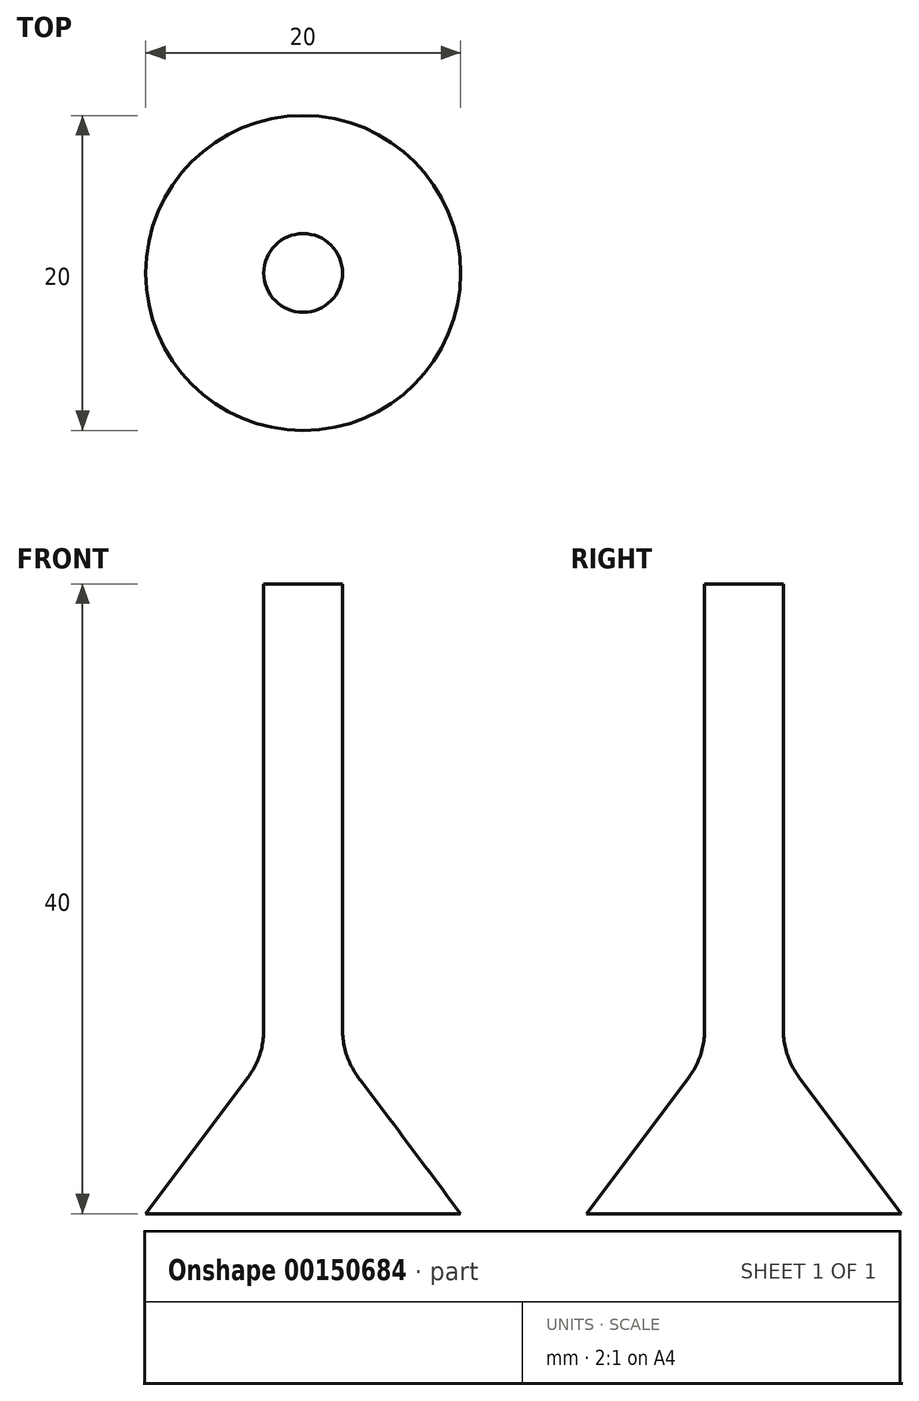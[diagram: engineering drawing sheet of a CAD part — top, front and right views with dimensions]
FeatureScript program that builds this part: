
annotation { "Feature Type Name" : "Feature", "Feature Type Description" : "" }
export const myFeature = defineFeature(function(context is Context, id is Id, definition is map)
    precondition{}
    {
        {
            var Q0;
            Q0=qCreatedBy(makeId("Front.planeOp"),FACE);
            var sketch = newSketch(context, id + "F0", { "sketchPlane" : qUnion([Q0])});
            skLineSegment(sketch, "E0.bottom", {"start": v(-2.96, 40.01) * mm, "end": v(-5.46, 40.01) * mm});
            skLineSegment(sketch, "E0.top", {"start": v(-2.96, 10.01) * mm, "end": v(-5.46, 10.01) * mm});
            skLineSegment(sketch, "E0.left", {"start": v(-2.96, 40.01) * mm, "end": v(-2.96, 10.01) * mm});
            skLineSegment(sketch, "E0.right", {"start": v(-5.46, 40.01) * mm, "end": v(-5.46, 11.68) * mm});
            skLineSegment(sketch, "E1", {"start": v(-2.96, 10.01) * mm, "end": v(-2.96, 0.01) * mm});
            skLineSegment(sketch, "E2", {"start": v(-2.96, 0.01) * mm, "end": v(-12.96, 0.01) * mm});
            skLineSegment(sketch, "E3", {"start": v(-12.96, 0.01) * mm, "end": v(-6.46, 8.68) * mm});
            skPoint(sketch, "E4.visualSharp", {"position": v(-5.46, 10.01) * mm});
            skArc(sketch, "E4.filletArc", {"start": v(-6.46, 8.68) * mm, "mid": v(-5.72, 10.1) * mm, "end": v(-5.46, 11.68) * mm});
            skSolve(sketch);
        }
        {
            var Q0;
            Q0=makeQuery(id+"F0.imprint","IMPRINT",FACE,{"disambiguationData":[TD([[makeQuery(id+"F0.imprint","IMPRINT",EDGE,{"derivedFrom":sQuery(id+"F0.wireOp",EDGE,"E0.bottom")}),1.0]])]});
            var Q1;
            Q1=makeQuery(id+"F0.imprint","IMPRINT",FACE,{"disambiguationData":[TD([[makeQuery(id+"F0.imprint","IMPRINT",EDGE,{"derivedFrom":sQuery(id+"F0.wireOp",EDGE,"E0.top")}),1.0]])]});
            var Q2;
            Q2=sQuery(id+"F0.wireOp",EDGE,"E0.left");
            revolve(context, id + "F1", {"entities" : qUnion([Q0, Q1]), "axis" : qUnion([Q2]), "revolveType" : RevolveType.FULL});
        }
    });
